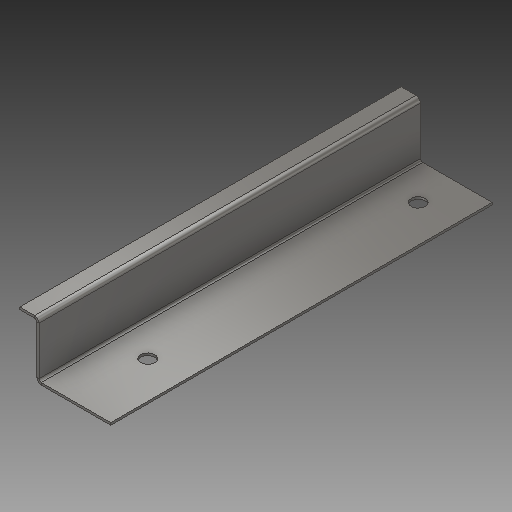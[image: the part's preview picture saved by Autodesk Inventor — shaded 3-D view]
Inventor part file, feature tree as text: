
AUTODESK INVENTOR PART (.ipt)
format: ipt  version: 2017 (Build 210142000, 142)  size: 146,944 bytes
history: native  units: in
note: dims shown in document units (in); Inventor stores cm internally (conversion verified against a paired STEP export)
features: other x3, sketch x2
ambient origin geometry x8: Origin, YZ Plane, XZ Plane, XY Plane, X Axis, Y Axis, Z Axis, Center Point
bodies: Solid1 (feature_tree)
feature tree (5):
  other  "Chapa Fixação Pé Nivelador.ipt"
  other  "Solid1::Chapa Fixação Pé Nivelador.ipt"
  other  "TaggingFeature1"
  sketch  "Sketch1"  dims[d0=0.3937in]
  sketch  "Sketch2"
